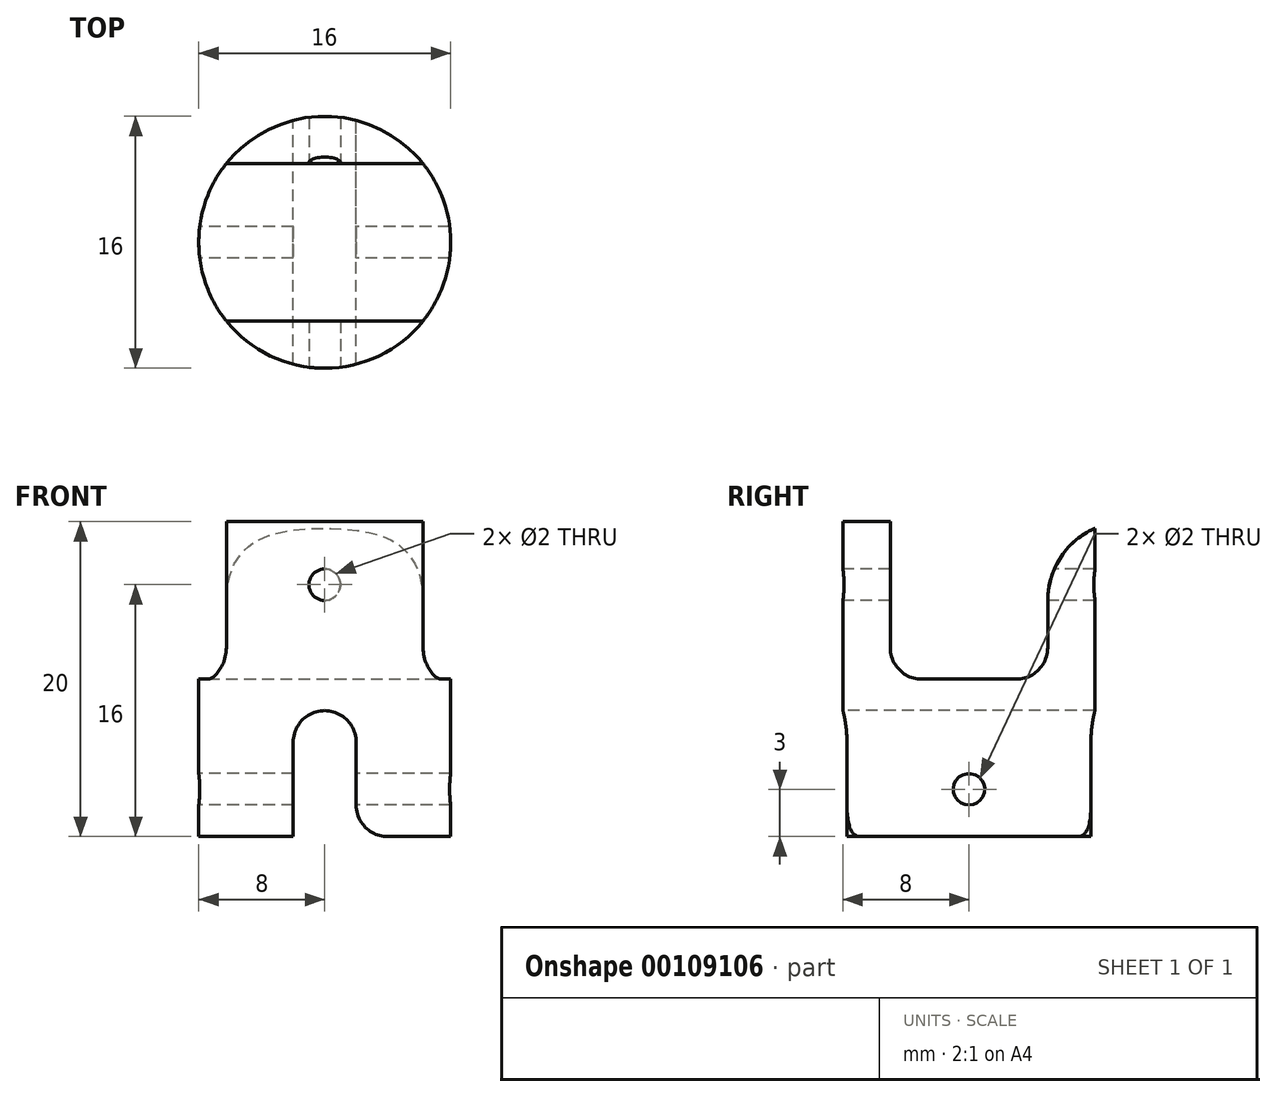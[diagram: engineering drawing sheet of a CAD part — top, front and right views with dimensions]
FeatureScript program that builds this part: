
annotation { "Feature Type Name" : "Feature", "Feature Type Description" : "" }
export const myFeature = defineFeature(function(context is Context, id is Id, definition is map)
    precondition{}
    {
        {
            var Q0;
            Q0=qCreatedBy(makeId("Top.planeOp"),FACE);
            var sketch = newSketch(context, id + "F0", { "sketchPlane" : qUnion([Q0])});
            skLineSegment(sketch, "E0.bottom", {"start": v(-8, 8) * mm, "end": v(8, 8) * mm});
            skLineSegment(sketch, "E0.top", {"start": v(-8, -8) * mm, "end": v(8, -8) * mm});
            skLineSegment(sketch, "E0.left", {"start": v(-8, 8) * mm, "end": v(-8, -8) * mm});
            skLineSegment(sketch, "E0.right", {"start": v(8, 8) * mm, "end": v(8, -8) * mm});
            skPoint(sketch, "E0.middle", {"position": v(0, 0) * mm});
            skSolve(sketch);
        }
        {
            var Q0;
            Q0=makeQuery(id+"F0.imprint","IMPRINT",FACE,{"disambiguationData":[TD([[makeQuery(id+"F0.imprint","IMPRINT",EDGE,{"derivedFrom":sQuery(id+"F0.wireOp",EDGE,"E0.bottom")}),-1.0]])]});
            extrude(context, id + "F1", {"entities" : qUnion([Q0]), "depth" : 20 * mm});
        }
        {
            var Q0;
            Q0=makeQuery(id+"F1.opExtrude","SWEPT_FACE",FACE,{"disambiguationData":[OSD([sQuery(id+"F0.wireOp",EDGE,"E0.top")])]});
            var sketch = newSketch(context, id + "F2", { "sketchPlane" : qUnion([Q0])});
            skLineSegment(sketch, "E1", {"start": v(0, 20) * mm, "end": v(0, 0) * mm});
            skCircle(sketch, "E2", {"center": v(0, 16) * mm, "radius": 1 * mm});
            skSolve(sketch);
        }
        {
            var Q0;
            Q0=sQuery(id+"F2.wireOp",VERTEX,"E2.center");
            var Q1;
            Q1=makeQuery(id+"F1.opExtrude","SWEPT_BODY",BODY,{"disambiguationData":[OSD([sQuery(id+"F0.wireOp",EDGE,"E0.bottom"),sQuery(id+"F0.wireOp",EDGE,"E0.top"),sQuery(id+"F0.wireOp",EDGE,"E0.left"),sQuery(id+"F0.wireOp",EDGE,"E0.right")])]});
            hole(context, id + "F3", {"style" : HoleStyle.SIMPLE, "endStyle" : HoleEndStyle.THROUGH, "holeDiameter" : 2 * mm, "locations" : qUnion([Q0]), "scope" : qUnion([Q1]), "isTappedThrough" : true});
        }
        {
            var Q0;
            Q0=makeQuery(id+"F1.opExtrude","SWEPT_FACE",FACE,{"disambiguationData":[OSD([sQuery(id+"F0.wireOp",EDGE,"E0.left")])]});
            var sketch = newSketch(context, id + "F4", { "sketchPlane" : qUnion([Q0])});
            skLineSegment(sketch, "E3", {"start": v(0, 20) * mm, "end": v(0, 0) * mm});
            skCircle(sketch, "E4", {"center": v(0, 3) * mm, "radius": 1 * mm});
            skSolve(sketch);
        }
        {
            var Q0;
            Q0=sQuery(id+"F4.wireOp",VERTEX,"E4.center");
            var Q1;
            Q1=makeQuery(id+"F1.opExtrude","SWEPT_BODY",BODY,{"disambiguationData":[OSD([sQuery(id+"F0.wireOp",EDGE,"E0.bottom"),sQuery(id+"F0.wireOp",EDGE,"E0.top"),sQuery(id+"F0.wireOp",EDGE,"E0.left"),sQuery(id+"F0.wireOp",EDGE,"E0.right")])]});
            hole(context, id + "F5", {"style" : HoleStyle.SIMPLE, "endStyle" : HoleEndStyle.THROUGH, "holeDiameter" : 2 * mm, "locations" : qUnion([Q0]), "scope" : qUnion([Q1]), "isTappedThrough" : true});
        }
        {
            var Q0;
            Q0=makeQuery(id+"F1.opExtrude","CAP_FACE",FACE,{"disambiguationData":[OSD([sQuery(id+"F0.wireOp",EDGE,"E0.bottom"),sQuery(id+"F0.wireOp",EDGE,"E0.top"),sQuery(id+"F0.wireOp",EDGE,"E0.left"),sQuery(id+"F0.wireOp",EDGE,"E0.right")])],"isStart":false});
            var sketch = newSketch(context, id + "F6", { "sketchPlane" : qUnion([Q0])});
            skCircle(sketch, "E5", {"center": v(0, 0) * mm, "radius": 8 * mm});
            skSolve(sketch);
        }
        {
            var Q0;
            {var subQ0=sQuery(id+"F6.wireOp",EDGE,"E5");var subQ1=makeQuery(id+"F1.opExtrude","CAP_EDGE",EDGE,{"disambiguationData":[OSD([sQuery(id+"F0.wireOp",EDGE,"E0.bottom")])],"isStart":false});var subQ2=makeQuery(id+"F6.imprint","INTERSECT",VERTEX,{"derivedFrom":[subQ1,subQ0]});Q0=makeQuery(id+"F6.imprint","IMPRINT",FACE,{"disambiguationData":[TD([[makeQuery(id+"F6.imprint","IMPRINT",EDGE,{"disambiguationData":[TD([[subQ2,-1.0]])],"derivedFrom":subQ0}),-1.0]])]});}
            var Q1;
            {var subQ0=sQuery(id+"F6.wireOp",EDGE,"E5");var subQ1=makeQuery(id+"F1.opExtrude","CAP_EDGE",EDGE,{"disambiguationData":[OSD([sQuery(id+"F0.wireOp",EDGE,"E0.bottom")])],"isStart":false});var subQ2=makeQuery(id+"F6.imprint","INTERSECT",VERTEX,{"derivedFrom":[subQ1,subQ0]});Q1=makeQuery(id+"F6.imprint","IMPRINT",FACE,{"disambiguationData":[TD([[makeQuery(id+"F6.imprint","IMPRINT",EDGE,{"disambiguationData":[TD([[subQ2,1.0]])],"derivedFrom":subQ0}),-1.0]])]});}
            var Q2;
            {var subQ0=sQuery(id+"F6.wireOp",EDGE,"E5");var subQ1=makeQuery(id+"F1.opExtrude","CAP_EDGE",EDGE,{"disambiguationData":[OSD([sQuery(id+"F0.wireOp",EDGE,"E0.right")])],"isStart":false});var subQ2=makeQuery(id+"F6.imprint","INTERSECT",VERTEX,{"derivedFrom":[subQ1,subQ0]});Q2=makeQuery(id+"F6.imprint","IMPRINT",FACE,{"disambiguationData":[TD([[makeQuery(id+"F6.imprint","IMPRINT",EDGE,{"disambiguationData":[TD([[subQ2,1.0]])],"derivedFrom":subQ0}),-1.0]])]});}
            var Q3;
            {var subQ0=sQuery(id+"F6.wireOp",EDGE,"E5");var subQ1=makeQuery(id+"F1.opExtrude","CAP_EDGE",EDGE,{"disambiguationData":[OSD([sQuery(id+"F0.wireOp",EDGE,"E0.left")])],"isStart":false});var subQ2=makeQuery(id+"F6.imprint","INTERSECT",VERTEX,{"derivedFrom":[subQ1,subQ0]});Q3=makeQuery(id+"F6.imprint","IMPRINT",FACE,{"disambiguationData":[TD([[makeQuery(id+"F6.imprint","IMPRINT",EDGE,{"disambiguationData":[TD([[subQ2,-1.0]])],"derivedFrom":subQ0}),-1.0]])]});}
            extrude(context, id + "F7", {"entities" : qUnion([Q0, Q1, Q2, Q3]), "operationType" : NewBodyOperationType.REMOVE, "oppositeDirection" : true, "depth" : 20 * mm});
        }
        {
            var Q0;
            Q0=makeQuery(id+"F1.opExtrude","CAP_FACE",FACE,{"disambiguationData":[OSD([sQuery(id+"F0.wireOp",EDGE,"E0.bottom"),sQuery(id+"F0.wireOp",EDGE,"E0.top"),sQuery(id+"F0.wireOp",EDGE,"E0.left"),sQuery(id+"F0.wireOp",EDGE,"E0.right")])],"isStart":false});
            var sketch = newSketch(context, id + "F8", { "sketchPlane" : qUnion([Q0])});
            skLineSegment(sketch, "E6.bottom", {"start": v(-6.24, 5) * mm, "end": v(6.24, 5) * mm});
            skLineSegment(sketch, "E6.top", {"start": v(-6.24, -5) * mm, "end": v(6.24, -5) * mm});
            skLineSegment(sketch, "E6.left", {"start": v(-6.24, 5) * mm, "end": v(-6.24, -5) * mm});
            skLineSegment(sketch, "E6.right", {"start": v(6.24, 5) * mm, "end": v(6.24, -5) * mm});
            skPoint(sketch, "E6.middle", {"position": v(0, 0) * mm});
            skSolve(sketch);
        }
        {
            var Q0;
            {var subQ0=sQuery(id+"F8.wireOp",EDGE,"E6.left");Q0=makeQuery(id+"F8.imprint","IMPRINT",FACE,{"disambiguationData":[TD([[makeQuery(id+"F8.imprint","IMPRINT",EDGE,{"derivedFrom":subQ0}),-1.0]])]});}
            var Q1;
            Q1=makeQuery(id+"F8.imprint","IMPRINT",FACE,{"disambiguationData":[TD([[makeQuery(id+"F8.imprint","IMPRINT",EDGE,{"derivedFrom":sQuery(id+"F8.wireOp",EDGE,"E6.bottom")}),-1.0]])]});
            var Q2;
            {var subQ0=sQuery(id+"F8.wireOp",EDGE,"E6.right");Q2=makeQuery(id+"F8.imprint","IMPRINT",FACE,{"disambiguationData":[TD([[makeQuery(id+"F8.imprint","IMPRINT",EDGE,{"derivedFrom":subQ0}),1.0]])]});}
            extrude(context, id + "F9", {"entities" : qUnion([Q0, Q1, Q2]), "operationType" : NewBodyOperationType.REMOVE, "oppositeDirection" : true, "depth" : 10 * mm});
        }
        {
            var Q0;
            Q0=makeQuery(id+"F9.boolean.opBoolean","COPY",EDGE,{"derivedFrom":makeQuery(id+"F9.opExtrude","CAP_EDGE",EDGE,{"disambiguationData":[OSD([sQuery(id+"F8.wireOp",EDGE,"E6.bottom")])],"isStart":true})});
            var Q1;
            Q1=makeQuery(id+"F9.boolean.opBoolean","COPY",EDGE,{"derivedFrom":makeQuery(id+"F9.opExtrude","CAP_EDGE",EDGE,{"disambiguationData":[OSD([sQuery(id+"F8.wireOp",EDGE,"E6.top")])],"isStart":true})});
            fillet(context, id + "F10", {"entities" : qUnion([Q0, Q1]), "radius" : 5 * mm, "tangentPropagation" : true, "allowEdgeOverflow" : false});
        }
        {
            var Q0;
            Q0=makeQuery(id+"F1.opExtrude","CAP_FACE",FACE,{"disambiguationData":[OSD([sQuery(id+"F0.wireOp",EDGE,"E0.bottom"),sQuery(id+"F0.wireOp",EDGE,"E0.top"),sQuery(id+"F0.wireOp",EDGE,"E0.left"),sQuery(id+"F0.wireOp",EDGE,"E0.right")])],"isStart":true});
            var sketch = newSketch(context, id + "F11", { "sketchPlane" : qUnion([Q0])});
            skLineSegment(sketch, "E7.bottom", {"start": v(-2, 7.75) * mm, "end": v(2, 7.75) * mm});
            skLineSegment(sketch, "E7.top", {"start": v(-2, -7.75) * mm, "end": v(2, -7.75) * mm});
            skLineSegment(sketch, "E7.left", {"start": v(-2, 7.75) * mm, "end": v(-2, -7.75) * mm});
            skLineSegment(sketch, "E7.right", {"start": v(2, 7.75) * mm, "end": v(2, -7.75) * mm});
            skPoint(sketch, "E7.middle", {"position": v(0, 0) * mm});
            skSolve(sketch);
        }
        {
            var Q0;
            {var subQ0=sQuery(id+"F11.wireOp",EDGE,"E7.bottom");Q0=makeQuery(id+"F11.imprint","IMPRINT",FACE,{"disambiguationData":[TD([[makeQuery(id+"F11.imprint","IMPRINT",EDGE,{"derivedFrom":subQ0}),1.0]])]});}
            var Q1;
            Q1=makeQuery(id+"F11.imprint","IMPRINT",FACE,{"disambiguationData":[TD([[makeQuery(id+"F11.imprint","IMPRINT",EDGE,{"derivedFrom":sQuery(id+"F11.wireOp",EDGE,"E7.bottom")}),-1.0]])]});
            var Q2;
            {var subQ0=sQuery(id+"F11.wireOp",EDGE,"E7.top");Q2=makeQuery(id+"F11.imprint","IMPRINT",FACE,{"disambiguationData":[TD([[makeQuery(id+"F11.imprint","IMPRINT",EDGE,{"derivedFrom":subQ0}),-1.0]])]});}
            extrude(context, id + "F12", {"entities" : qUnion([Q0, Q1, Q2]), "operationType" : NewBodyOperationType.REMOVE, "oppositeDirection" : true, "depth" : 8 * mm});
        }
        {
            var Q0;
            Q0=makeQuery(id+"F12.boolean.opBoolean","COPY",EDGE,{"derivedFrom":makeQuery(id+"F12.opExtrude","CAP_EDGE",EDGE,{"disambiguationData":[OSD([sQuery(id+"F11.wireOp",EDGE,"E7.left")])],"isStart":true})});
            var Q1;
            Q1=makeQuery(id+"F12.boolean.opBoolean","COPY",EDGE,{"derivedFrom":makeQuery(id+"F12.opExtrude","CAP_EDGE",EDGE,{"disambiguationData":[OSD([sQuery(id+"F11.wireOp",EDGE,"E7.right")])],"isStart":true})});
            fillet(context, id + "F13", {"entities" : qUnion([Q0, Q1]), "radius" : 2 * mm, "tangentPropagation" : true, "allowEdgeOverflow" : false});
        }
        {
            var Q0;
            Q0=makeQuery(id+"F9.boolean.opBoolean","COPY",EDGE,{"derivedFrom":makeQuery(id+"F9.opExtrude","CAP_EDGE",EDGE,{"disambiguationData":[OSD([sQuery(id+"F8.wireOp",EDGE,"E6.top")])],"isStart":false})});
            var Q1;
            Q1=makeQuery(id+"F9.boolean.opBoolean","COPY",EDGE,{"derivedFrom":makeQuery(id+"F9.opExtrude","CAP_EDGE",EDGE,{"disambiguationData":[OSD([sQuery(id+"F8.wireOp",EDGE,"E6.bottom")])],"isStart":false})});
            var Q2;
            Q2=makeQuery(id+"F12.boolean.opBoolean","COPY",EDGE,{"derivedFrom":makeQuery(id+"F12.opExtrude","CAP_EDGE",EDGE,{"disambiguationData":[OSD([sQuery(id+"F11.wireOp",EDGE,"E7.right")])],"isStart":false})});
            var Q3;
            Q3=makeQuery(id+"F12.boolean.opBoolean","COPY",EDGE,{"derivedFrom":makeQuery(id+"F12.opExtrude","CAP_EDGE",EDGE,{"disambiguationData":[OSD([sQuery(id+"F11.wireOp",EDGE,"E7.left")])],"isStart":false})});
            fillet(context, id + "F14", {"entities" : qUnion([Q0, Q1, Q2, Q3]), "radius" : 2 * mm, "tangentPropagation" : true, "allowEdgeOverflow" : false});
        }
    });
